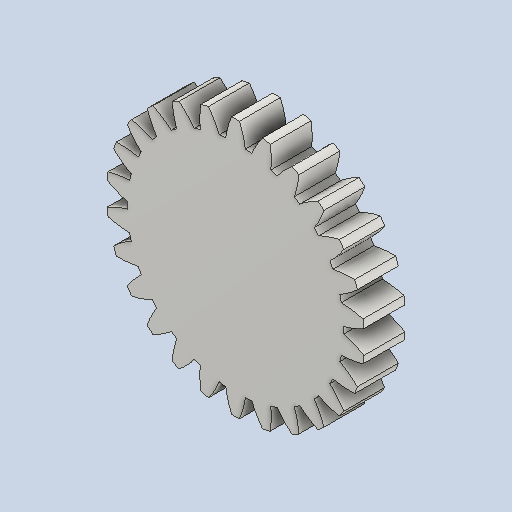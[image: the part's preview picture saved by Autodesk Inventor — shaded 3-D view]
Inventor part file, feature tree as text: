
AUTODESK INVENTOR PART (.ipt)
format: ipt  version: 2024 (Build 280153000, 153)  size: 253,440 bytes
history: native  units: mm (DEFAULTED — no unit token found)
features: plane x3, other x3, extrude x1, sketch x1
ambient origin geometry x8: Origin, YZ Plane, XZ Plane, XY Plane, X Axis, Y Axis, Z Axis, Center Point
bodies: Solid1 (feature_tree)
feature tree (8):
  extrude  "Extrusion1"  Depth=20.0mm TaperAngle=0.0deg
  plane  "Work Plane2"
  plane  "Work Plane8"
  plane  "Work Plane9"
  other  "Spur Gear"
  sketch  "Sketch1"  dims[d0=125.986639mm d1=20.0mm d2=0.0mm d3=117.0mm d4=10.0mm d5=0.0mm d16=140.0mm d17=0.0mm d34=1.208305mm d39=0.0mm d41=0.0mm d43=140.0mm d46=140.0mm d47=0.0mm d48=0.0mm]
  other  "Srf1"
  other  "Pitch Diameter"
